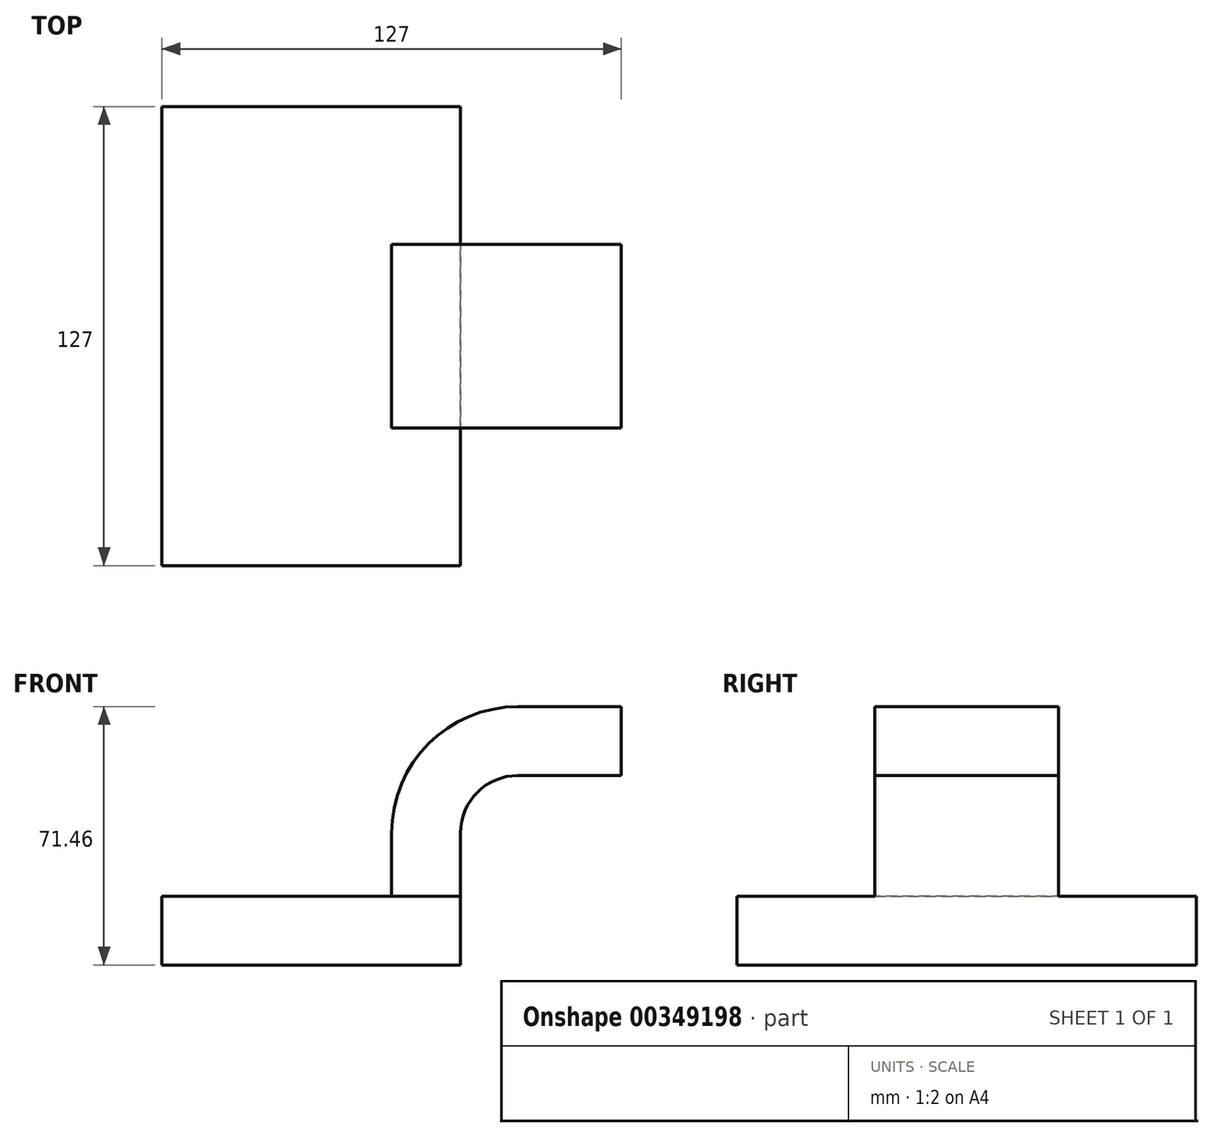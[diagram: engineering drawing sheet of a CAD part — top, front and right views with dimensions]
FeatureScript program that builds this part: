
annotation { "Feature Type Name" : "Feature", "Feature Type Description" : "" }
export const myFeature = defineFeature(function(context is Context, id is Id, definition is map)
    precondition{}
    {
        {
            var Q0;
            Q0=qCreatedBy(makeId("Front.planeOp"),FACE);
            var sketch = newSketch(context, id + "F0", { "sketchPlane" : qUnion([Q0])});
            skLineSegment(sketch, "E0.bottom", {"start": v(41.28, -9.52) * mm, "end": v(-41.28, -9.53) * mm});
            skLineSegment(sketch, "E0.top", {"start": v(41.28, 9.53) * mm, "end": v(-41.28, 9.53) * mm});
            skLineSegment(sketch, "E0.left", {"start": v(41.28, -9.52) * mm, "end": v(41.28, 9.53) * mm});
            skLineSegment(sketch, "E0.right", {"start": v(-41.28, -9.53) * mm, "end": v(-41.28, 9.53) * mm});
            skPoint(sketch, "E0.middle", {"position": v(0, 0) * mm});
            skLineSegment(sketch, "E1.bottom", {"start": v(111.12, 38.1) * mm, "end": v(60.32, 38.1) * mm});
            skLineSegment(sketch, "E1.top", {"start": v(111.12, 66.68) * mm, "end": v(60.32, 66.68) * mm});
            skLineSegment(sketch, "E1.left", {"start": v(111.12, 38.1) * mm, "end": v(111.12, 66.68) * mm});
            skLineSegment(sketch, "E1.right", {"start": v(60.32, 38.1) * mm, "end": v(60.32, 66.68) * mm});
            skPoint(sketch, "E1.middle", {"position": v(85.72, 52.39) * mm});
            skLineSegment(sketch, "E2", {"start": v(41.28, 9.53) * mm, "end": v(41.28, 27) * mm});
            skArc(sketch, "E3", {"start": v(41.27, 27) * mm, "mid": v(45.92, 38.23) * mm, "end": v(57.15, 42.88) * mm});
            skLineSegment(sketch, "E4", {"start": v(57.15, 42.88) * mm, "end": v(85.72, 42.88) * mm});
            skLineSegment(sketch, "E5.0", {"start": v(57.15, 61.93) * mm, "end": v(85.72, 61.93) * mm});
            skArc(sketch, "E5.1", {"start": v(22.23, 27) * mm, "mid": v(32.45, 51.7) * mm, "end": v(57.15, 61.93) * mm});
            skLineSegment(sketch, "E5.2", {"start": v(22.22, 9.53) * mm, "end": v(22.22, 27) * mm});
            skLineSegment(sketch, "E6", {"start": v(85.72, 66.68) * mm, "end": v(85.72, 38.1) * mm});
            skFitSpline(sketch, "E7", {"points": [v(-41.28, 9.53) * mm, v(57.15, 61.93) * mm], "startDerivative": vector(0.06, 78.65) * mm, "endDerivative": vector(139.44, -1.47) * mm});
            skSolve(sketch);
        }
        {
            var Q0;
            Q0=makeQuery(id+"F0.imprint","IMPRINT",FACE,{"disambiguationData":[TD([[makeQuery(id+"F0.imprint","IMPRINT",EDGE,{"derivedFrom":sQuery(id+"F0.wireOp",EDGE,"E0.bottom")}),-1.0]])]});
            extrude(context, id + "F1", {"entities" : qUnion([Q0]), "oppositeDirection" : true, "depth" : 127 * mm, "symmetric" : true});
        }
        {
            var Q0;
            {var subQ1=sQuery(id+"F0.wireOp",EDGE,"E2");Q0=makeQuery(id+"F0.imprint","IMPRINT",FACE,{"disambiguationData":[TD([[makeQuery(id+"F0.imprint","IMPRINT",EDGE,{"derivedFrom":subQ1}),1.0]])]});}
            var Q1;
            {var subQ0=sQuery(id+"F0.wireOp",EDGE,"E4");var subQ1=sQuery(id+"F0.wireOp",EDGE,"E1.right");var subQ2=makeQuery(id+"F0.imprint","INTERSECT",VERTEX,{"derivedFrom":[subQ1,subQ0]});Q1=makeQuery(id+"F0.imprint","IMPRINT",FACE,{"disambiguationData":[TD([[makeQuery(id+"F0.imprint","IMPRINT",EDGE,{"disambiguationData":[TD([[subQ2,-1.0]])],"derivedFrom":subQ1}),-1.0]])]});}
            extrude(context, id + "F2", {"entities" : qUnion([Q0, Q1]), "operationType" : NewBodyOperationType.ADD, "depth" : 50.8 * mm, "symmetric" : true});
        }
        {
            var Q0;
            Q0=makeQuery(id+"F0.imprint","IMPRINT",FACE,{"disambiguationData":[TD([[makeQuery(id+"F0.imprint","IMPRINT",EDGE,{"derivedFrom":sQuery(id+"F0.wireOp",EDGE,"E5.1")}),1.0]])]});
            extrude(context, id + "F3", {"entities" : qUnion([Q0]), "operationType" : NewBodyOperationType.ADD, "depth" : 15.88 * mm, "symmetric" : true});
        }
    });
